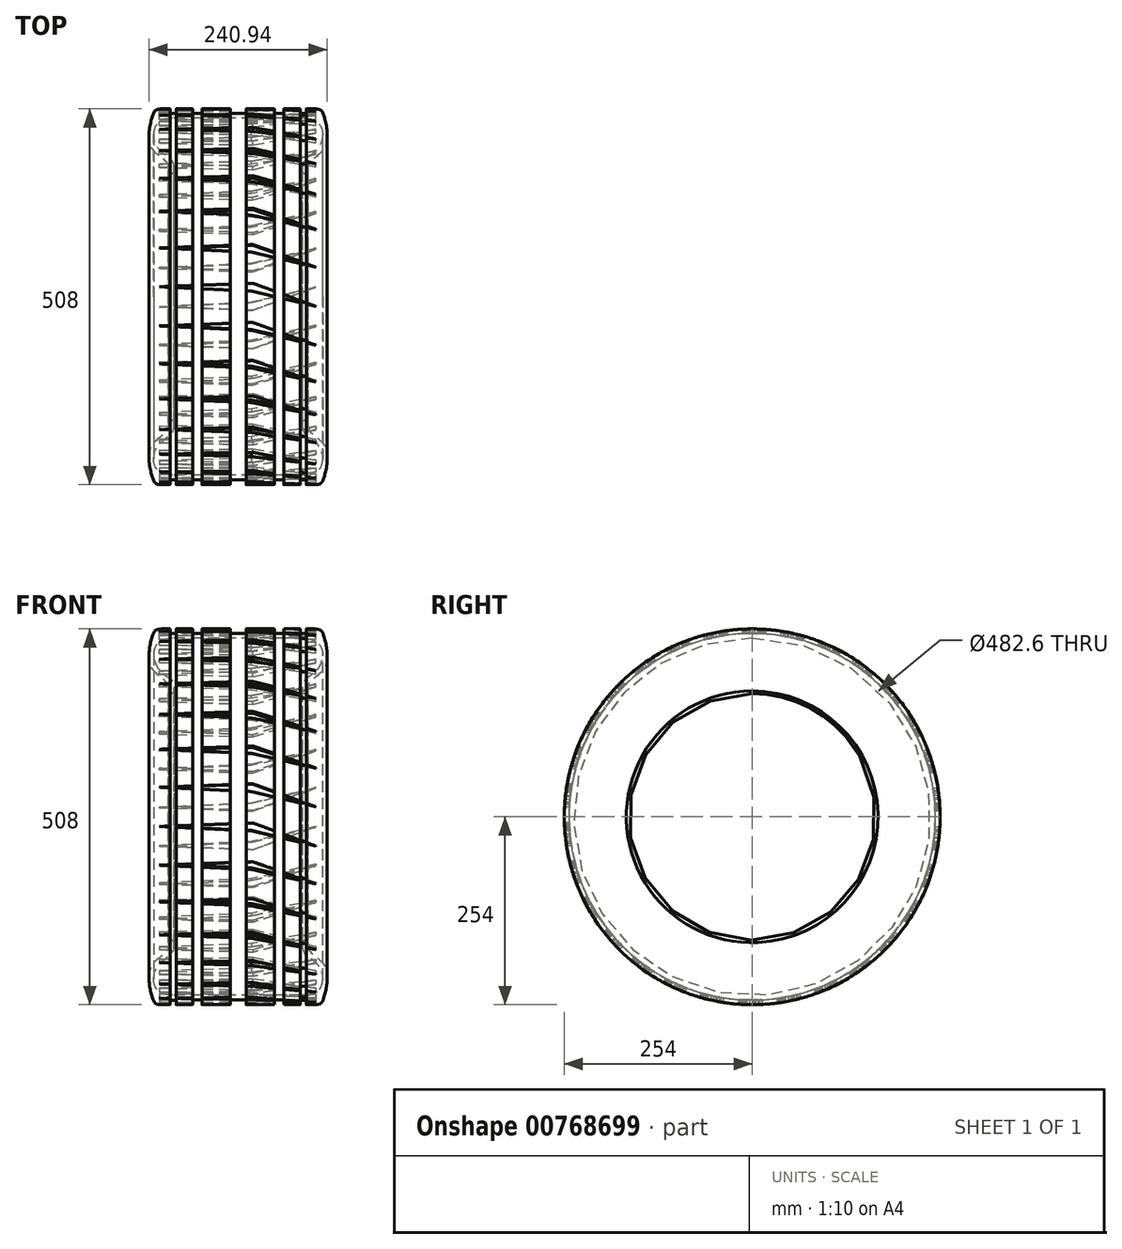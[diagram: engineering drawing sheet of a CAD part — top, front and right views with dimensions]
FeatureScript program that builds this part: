
annotation { "Feature Type Name" : "Feature", "Feature Type Description" : "" }
export const myFeature = defineFeature(function(context is Context, id is Id, definition is map)
    precondition{}
    {
        {
            var Q0;
            Q0=qCreatedBy(makeId("Front.planeOp"),FACE);
            var sketch = newSketch(context, id + "F0", { "sketchPlane" : qUnion([Q0])});
            skLineSegment(sketch, "E0", {"start": v(0, 0) * mm, "end": v(101.6, 0) * mm});
            skLineSegment(sketch, "E1", {"start": v(0, 12.7) * mm, "end": v(88.9, 12.7) * mm});
            skLineSegment(sketch, "E2", {"start": v(0, 12.7) * mm, "end": v(0, 0) * mm});
            skFitSpline(sketch, "E3", {"points": [v(88.9, 12.7) * mm, v(113.31, 27.68) * mm, v(106.52, 55.25) * mm, v(88.9, 70.88) * mm, v(86.77, 83.85) * mm], "startDerivative": vector(148.91, -0.67) * mm, "endDerivative": vector(0.67, 65.93) * mm});
            skFitSpline(sketch, "E4", {"points": [v(101.6, 0) * mm, v(114.96, 7.1) * mm, v(118.04, 49.9) * mm, v(96.23, 72.94) * mm, v(94.18, 83.85) * mm], "startDerivative": vector(147.56, 0) * mm, "endDerivative": vector(4.13, 64.2) * mm});
            skArc(sketch, "E5", {"start": v(94.18, 83.85) * mm, "mid": v(90.47, 87.4) * mm, "end": v(86.77, 83.85) * mm});
            skLineSegment(sketch, "E6", {"start": v(-94.18, 254) * mm, "end": v(94.18, 254) * mm});
            skLineSegment(sketch, "E7.MirrorCS", {"start": v(0, 0) * mm, "end": v(-101.6, 0) * mm});
            skLineSegment(sketch, "E8.MirrorCS", {"start": v(0, 12.7) * mm, "end": v(-88.9, 12.7) * mm});
            skFitSpline(sketch, "E9.MirrorCS", {"points": [v(-88.9, 12.7) * mm, v(-113.31, 27.68) * mm, v(-106.52, 55.25) * mm, v(-88.9, 70.88) * mm, v(-86.77, 83.85) * mm], "startDerivative": vector(-148.91, -0.67) * mm, "endDerivative": vector(-0.67, 65.93) * mm});
            skFitSpline(sketch, "E10.MirrorCS", {"points": [v(-101.6, 0) * mm, v(-114.96, 7.1) * mm, v(-118.04, 49.9) * mm, v(-96.23, 72.94) * mm, v(-94.18, 83.85) * mm], "startDerivative": vector(-147.56, 0) * mm, "endDerivative": vector(-4.13, 64.2) * mm});
            skArc(sketch, "E11.MirrorCS", {"start": v(-94.18, 83.85) * mm, "mid": v(-90.47, 87.4) * mm, "end": v(-86.77, 83.85) * mm});
            skSolve(sketch);
        }
        {
            var Q0;
            Q0=qSketchRegion(id+"F0",true);
            var Q1;
            Q1=sQuery(id+"F0.wireOp",EDGE,"E6");
            revolve(context, id + "F1", {"entities" : qUnion([Q0]), "axis" : qUnion([Q1]), "revolveType" : RevolveType.FULL});
        }
        {
            var Q0;
            Q0=qCreatedBy(makeId("Front.planeOp"),FACE);
            var sketch = newSketch(context, id + "F2", { "sketchPlane" : qUnion([Q0])});
            skLineSegment(sketch, "E12", {"start": v(-10.8, 6.35) * mm, "end": v(-10.8, 0) * mm});
            skLineSegment(sketch, "E13", {"start": v(-48.9, 6.35) * mm, "end": v(-48.9, 0) * mm});
            skLineSegment(sketch, "E14", {"start": v(-61.6, 6.35) * mm, "end": v(-61.6, 0) * mm});
            skLineSegment(sketch, "E15", {"start": v(-92.08, 6.24) * mm, "end": v(-92.08, 0) * mm});
            skLineSegment(sketch, "E16", {"start": v(-83.82, 6.24) * mm, "end": v(-83.82, 0) * mm});
            skLineSegment(sketch, "E17.MirrorCS", {"start": v(10.8, 6.35) * mm, "end": v(10.8, 0) * mm});
            skLineSegment(sketch, "E18.MirrorCS", {"start": v(48.9, 6.35) * mm, "end": v(48.9, 0) * mm});
            skLineSegment(sketch, "E19.MirrorCS", {"start": v(61.6, 6.35) * mm, "end": v(61.6, 0) * mm});
            skLineSegment(sketch, "E20.MirrorCS", {"start": v(83.82, 6.24) * mm, "end": v(83.82, 0) * mm});
            skLineSegment(sketch, "E21.MirrorCS", {"start": v(92.08, 6.24) * mm, "end": v(92.08, 0) * mm});
            skLineSegment(sketch, "E22", {"start": v(83.82, 6.24) * mm, "end": v(92.08, 6.24) * mm});
            skLineSegment(sketch, "E23", {"start": v(-92.08, 6.24) * mm, "end": v(-83.82, 6.24) * mm});
            skLineSegment(sketch, "E24", {"start": v(-162.71, 254) * mm, "end": v(142.5, 254) * mm});
            skLineSegment(sketch, "E25", {"start": v(-92.08, 0) * mm, "end": v(-83.82, 0) * mm});
            skLineSegment(sketch, "E26", {"start": v(-61.6, 0) * mm, "end": v(-48.9, 0) * mm});
            skLineSegment(sketch, "E27", {"start": v(-10.8, 0) * mm, "end": v(10.8, 0) * mm});
            skLineSegment(sketch, "E28", {"start": v(48.9, 0) * mm, "end": v(61.6, 0) * mm});
            skLineSegment(sketch, "E29", {"start": v(83.82, 0) * mm, "end": v(92.08, 0) * mm});
            skLineSegment(sketch, "E30", {"start": v(-61.6, 6.35) * mm, "end": v(-48.9, 6.35) * mm});
            skLineSegment(sketch, "E31", {"start": v(-10.8, 6.35) * mm, "end": v(10.8, 6.35) * mm});
            skLineSegment(sketch, "E32", {"start": v(48.9, 6.35) * mm, "end": v(61.6, 6.35) * mm});
            skSolve(sketch);
        }
        {
            var Q0;
            Q0=qSketchRegion(id+"F2",true);
            var Q1;
            Q1=sQuery(id+"F2.wireOp",EDGE,"E24");
            revolve(context, id + "F3", {"operationType" : NewBodyOperationType.REMOVE, "entities" : qUnion([Q0]), "axis" : qUnion([Q1]), "revolveType" : RevolveType.FULL, "oppositeDirection" : true});
        }
        {
            var Q0;
            Q0=sQuery(id+"F2.wireOp",EDGE,"E24");
            var Q1;
            Q1=sQuery(id+"F2.wireOp",VERTEX,"E12.end");
            cPlane(context, id + "F4", {"entities" : qUnion([Q0, Q1]), "cplaneType" : CPlaneType.LINE_ANGLE, "offset" : 25.4 * mm, "angle" : 90 * degree, "width" : 152.4 * mm, "height" : 152.4 * mm});
        }
        {
            var Q0;
            Q0=qCreatedBy(id+"F4.planeOp",FACE);
            cPlane(context, id + "F5", {"entities" : qUnion([Q0]), "cplaneType" : CPlaneType.OFFSET, "offset" : 254 * mm, "width" : 152.4 * mm, "height" : 152.4 * mm});
        }
        {
            var Q0;
            Q0=qCreatedBy(id+"F5.planeOp",FACE);
            var sketch = newSketch(context, id + "F6", { "sketchPlane" : qUnion([Q0])});
            skLineSegment(sketch, "E33", {"start": v(-106.36, 13.56) * mm, "end": v(20.09, 18.26) * mm});
            skLineSegment(sketch, "E34", {"start": v(20.09, 18.26) * mm, "end": v(105.22, -13.04) * mm});
            skLineSegment(sketch, "E35", {"start": v(105.22, -13.04) * mm, "end": v(18.2, 7.62) * mm});
            skLineSegment(sketch, "E36", {"start": v(18.2, 7.62) * mm, "end": v(-106.36, 13.56) * mm});
            skSolve(sketch);
        }
        {
            var Q0;
            Q0=makeQuery(id+"F6.imprint","IMPRINT",FACE,{"disambiguationData":[TD([[makeQuery(id+"F6.imprint","IMPRINT",EDGE,{"derivedFrom":sQuery(id+"F6.wireOp",EDGE,"E33")}),-1.0]])]});
            extrude(context, id + "F7", {"entities" : qUnion([Q0]), "oppositeDirection" : true, "depth" : 6.35 * mm});
        }
        {
            var Q0;
            Q0=makeQuery(id+"F7.opExtrude","SWEPT_BODY",BODY,{"disambiguationData":[OSD([sQuery(id+"F6.wireOp",EDGE,"E33"),sQuery(id+"F6.wireOp",EDGE,"E34"),sQuery(id+"F6.wireOp",EDGE,"E35"),sQuery(id+"F6.wireOp",EDGE,"E36")])]});
            var Q1;
            Q1=sQuery(id+"F2.wireOp",EDGE,"E24");
            circularPattern(context, id + "F8", {"operationType" : NewBodyOperationType.REMOVE, "entities" : qUnion([Q0]), "axis" : qUnion([Q1]), "angle" : 360 * degree, "instanceCount" : 30, "equalSpace" : true});
        }
    });
